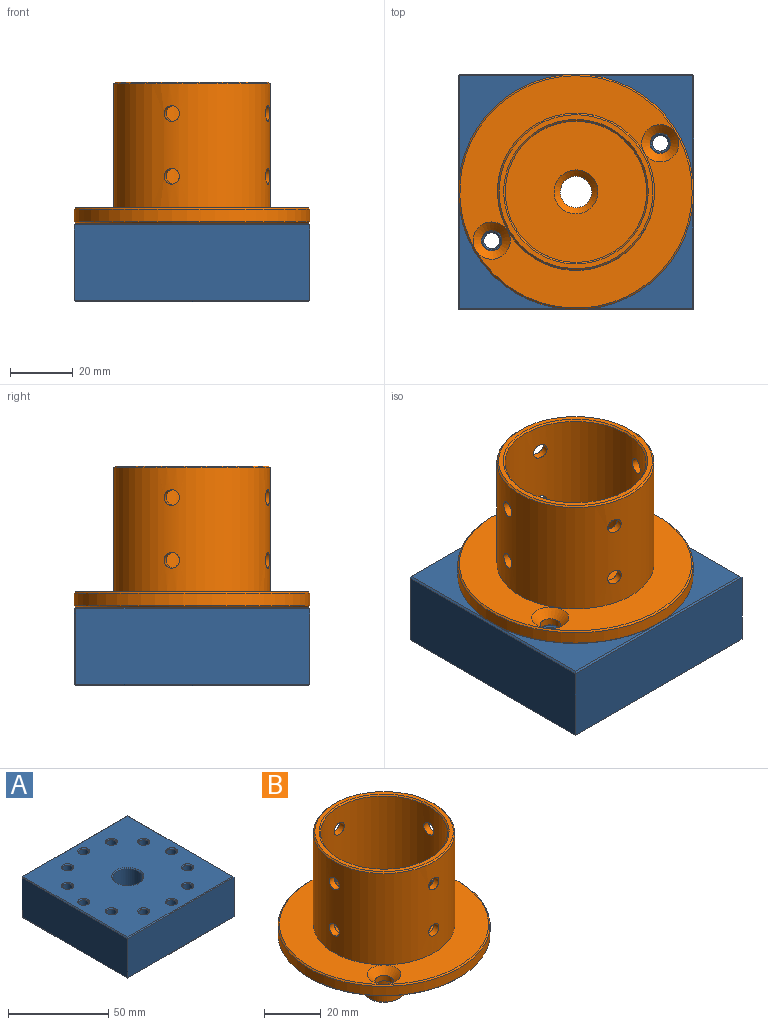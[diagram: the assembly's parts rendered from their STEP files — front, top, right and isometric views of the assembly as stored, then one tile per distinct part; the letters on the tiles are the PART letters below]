
ASSEMBLY  parts=2 mates=1
PART A: 59 faces, bbox 75x75x25 mm
  f0: plane 74x24mm, normal (0,1,0), area 1776mm2, adj f48,f52,f55,f58
  f1: plane 74.5x24mm, normal (-1,0,0), area 1788mm2, adj f2,f46,f52,f53
  f2: plane 75x24mm, normal (0,-1,0), area 1800mm2, adj f1,f4,f45,f50
  f3: cylinder r=7.5mm len=24mm, axis (0,0,-1), area 1131mm2, adj f43,f44
  f4: plane 74.5x24mm, normal (1,0,0), area 1788mm2, adj f2,f47,f54,f55
  f5: plane 74x74mm, normal (0,0,1), area 4935.6mm2, adj f31,f32,f33,f34,f35,f36,f37,f38
  f6: plane 74x74mm, normal (0,0,-1), area 4935.6mm2, adj f19,f20,f21,f22,f23,f24,f25,f26
  f7: cylinder r=2.5mm len=24mm, axis (0,0,1), area 377mm2, adj f20,f41
  f8: cylinder r=2.5mm len=24mm, axis (0,0,1), area 377mm2, adj f19,f42
  f9: cylinder r=2.5mm len=24mm, axis (0,0,1), area 377mm2, adj f30,f31
  f10: cylinder r=2.5mm len=24mm, axis (0,0,1), area 377mm2, adj f29,f32
  f11: cylinder r=2.5mm len=24mm, axis (0,0,1), area 377mm2, adj f21,f40
  f12: cylinder r=2.5mm len=24mm, axis (0,0,1), area 377mm2, adj f22,f39
  f13: cylinder r=2.5mm len=24mm, axis (0,0,1), area 377mm2, adj f23,f38
  f14: cylinder r=2.5mm len=24mm, axis (0,0,1), area 377mm2, adj f24,f37
  f15: cylinder r=2.5mm len=24mm, axis (0,0,1), area 377mm2, adj f25,f36
  f16: cylinder r=2.5mm len=24mm, axis (0,0,1), area 377mm2, adj f26,f35
  f17: cylinder r=2.5mm len=24mm, axis (0,0,1), area 377mm2, adj f27,f34
  f18: cylinder r=2.5mm len=24mm, axis (0,0,1), area 377mm2, adj f28,f33
  f19: cone r=3mm half-angle=45deg, axis (0,0,-1), area 12.2mm2, adj f6,f8
  f20: cone r=3mm half-angle=45deg, axis (0,0,-1), area 12.2mm2, adj f6,f7
  f21: cone r=3mm half-angle=45deg, axis (0,0,-1), area 12.2mm2, adj f6,f11
  f22: cone r=3mm half-angle=45deg, axis (0,0,-1), area 12.2mm2, adj f6,f12
  f23: cone r=3mm half-angle=45deg, axis (0,0,-1), area 12.2mm2, adj f6,f13
  f24: cone r=3mm half-angle=45deg, axis (0,0,-1), area 12.2mm2, adj f6,f14
  f25: cone r=3mm half-angle=45deg, axis (0,0,-1), area 12.2mm2, adj f6,f15
  f26: cone r=3mm half-angle=45deg, axis (0,0,-1), area 12.2mm2, adj f6,f16
  f27: cone r=3mm half-angle=45deg, axis (0,0,-1), area 12.2mm2, adj f6,f17
  f28: cone r=3mm half-angle=45deg, axis (0,0,-1), area 12.2mm2, adj f6,f18
  f29: cone r=3mm half-angle=45deg, axis (0,0,-1), area 12.2mm2, adj f6,f10
  f30: cone r=3mm half-angle=45deg, axis (0,0,-1), area 12.2mm2, adj f6,f9
  f31: cone r=2.5mm half-angle=45deg, axis (0,0,1), area 12.2mm2, adj f5,f9
  f32: cone r=2.5mm half-angle=45deg, axis (0,0,1), area 12.2mm2, adj f5,f10
  f33: cone r=2.5mm half-angle=45deg, axis (0,0,1), area 12.2mm2, adj f5,f18
  f34: cone r=2.5mm half-angle=45deg, axis (0,0,1), area 12.2mm2, adj f5,f17
  f35: cone r=2.5mm half-angle=45deg, axis (0,0,1), area 12.2mm2, adj f5,f16
  f36: cone r=2.5mm half-angle=45deg, axis (0,0,1), area 12.2mm2, adj f5,f15
  f37: cone r=2.5mm half-angle=45deg, axis (0,0,1), area 12.2mm2, adj f5,f14
  f38: cone r=2.5mm half-angle=45deg, axis (0,0,1), area 12.2mm2, adj f5,f13
  f39: cone r=2.5mm half-angle=45deg, axis (0,0,1), area 12.2mm2, adj f5,f12
  f40: cone r=2.5mm half-angle=45deg, axis (0,0,1), area 12.2mm2, adj f5,f11
  f41: cone r=2.5mm half-angle=45deg, axis (0,0,1), area 12.2mm2, adj f5,f7
  f42: cone r=2.5mm half-angle=45deg, axis (0,0,1), area 12.2mm2, adj f5,f8
  f43: cone r=8mm half-angle=45deg, axis (0,0,-1), area 34.4mm2, adj f3,f6
  f44: cone r=7.5mm half-angle=45deg, axis (0,0,1), area 34.4mm2, adj f3,f5
  f45: plane 75x0.5mm, normal (0,-0.71,0.71), area 52.7mm2, adj f2,f5,f46,f47
  f46: plane 74.5x0.5mm, normal (-0.71,0,0.71), area 52.5mm2, adj f1,f5,f45,f49
  f47: plane 74.5x0.5mm, normal (0.71,0,0.71), area 52.5mm2, adj f4,f5,f45,f51
  f48: plane 74x0.5mm, normal (0,0.71,0.71), area 52.3mm2, adj f0,f5,f49,f51
  f49: plane 0.5x0.5mm, normal (-0.58,0.58,0.58), area 0.2mm2, adj f46,f48,f52
  f50: plane 75x0.5mm, normal (0,-0.71,-0.71), area 52.7mm2, adj f2,f6,f53,f54
  f51: plane 0.5x0.5mm, normal (0.58,0.58,0.58), area 0.2mm2, adj f47,f48,f55
  f52: plane 24x0.5mm, normal (-0.71,0.71,0), area 17mm2, adj f0,f1,f49,f56
  f53: plane 74.5x0.5mm, normal (-0.71,0,-0.71), area 52.5mm2, adj f1,f6,f50,f56
  f54: plane 74.5x0.5mm, normal (0.71,0,-0.71), area 52.5mm2, adj f4,f6,f50,f57
  f55: plane 24x0.5mm, normal (0.71,0.71,0), area 17mm2, adj f0,f4,f51,f57
  f56: plane 0.5x0.5mm, normal (-0.58,0.58,-0.58), area 0.2mm2, adj f52,f53,f58
  f57: plane 0.5x0.5mm, normal (0.58,0.58,-0.58), area 0.2mm2, adj f54,f55,f58
  f58: plane 74x0.5mm, normal (0,0.71,-0.71), area 52.3mm2, adj f0,f6,f56,f57
PART B: 29 faces, bbox 75x75x69 mm
  f0: cylinder r=22.5mm len=45mm, axis (0,0,-1), area 5426.6mm2, adj f2,f12,f13,f14,f15,f16,f17,f18
  f1: cylinder r=25mm len=50mm, axis (0,0,-1), area 6047.1mm2, adj f5,f12,f13,f14,f15,f16,f17,f18
  f2: plane 45x45mm, normal (0,0,1), area 1436.5mm2, adj f0,f22
  f3: cylinder r=37.5mm len=75mm, axis (0,0,-1), area 942.5mm2, adj f25,f26
  f4: cylinder r=5mm len=26.5mm, axis (0,0,-1), area 832.5mm2, adj f22,f23
  f5: plane 74x74mm, normal (0,0,1), area 2116.4mm2, adj f1,f8,f10,f26
  f6: plane 74x74mm, normal (0,0,-1), area 4057.8mm2, adj f7,f9,f20,f25
  f7: cylinder r=3.25mm len=6.5mm, axis (0,0,1), area 47.4mm2, adj f6,f8
  f8: cone r=3.25mm half-angle=45deg, axis (0,0,1), area 109.3mm2, adj f5,f7
  f9: cylinder r=3.25mm len=6.5mm, axis (0,0,1), area 47.4mm2, adj f6,f10
  f10: cone r=3.25mm half-angle=45deg, axis (0,0,1), area 109.3mm2, adj f5,f9
  f11: plane 49x49mm, normal (0,0,1), area 223.8mm2, adj f27,f28
  f12: cylinder r=2.5mm len=5mm, axis (1,0,0), area 39.4mm2, adj f0,f1
  f13: cylinder r=2.5mm len=5mm, axis (1,0,0), area 39.4mm2, adj f0,f1
  f14: cylinder r=2.5mm len=5mm, axis (0,1,0), area 39.4mm2, adj f0,f1
  f15: cylinder r=2.5mm len=5mm, axis (0,1,0), area 39.4mm2, adj f0,f1
  f16: cylinder r=2.5mm len=5mm, axis (-1,0,0), area 39.4mm2, adj f0,f1
  f17: cylinder r=2.5mm len=5mm, axis (-1,0,0), area 39.4mm2, adj f0,f1
  f18: cylinder r=2.5mm len=5mm, axis (0,-1,0), area 39.4mm2, adj f0,f1
  f19: cylinder r=2.5mm len=5mm, axis (0,-1,0), area 39.4mm2, adj f0,f1
  f20: cylinder r=7.5mm len=23.5mm, axis (0,0,-1), area 1107.4mm2, adj f6,f24
  f21: plane 14x14mm, normal (0,0,-1), area 58.9mm2, adj f23,f24
  f22: cone r=5mm half-angle=45deg, axis (0,0,1), area 106.6mm2, adj f2,f4
  f23: cone r=5.5mm half-angle=45deg, axis (0,0,-1), area 23.3mm2, adj f4,f21
  f24: cone r=7.5mm half-angle=45deg, axis (0,0,1), area 32.2mm2, adj f20,f21
  f25: cone r=37.5mm half-angle=45deg, axis (0,0,1), area 165.5mm2, adj f3,f6
  f26: cone r=37mm half-angle=45deg, axis (0,0,-1), area 165.5mm2, adj f3,f5
  f27: cone r=24.5mm half-angle=45deg, axis (0,0,-1), area 110mm2, adj f1,f11
  f28: cone r=22.5mm half-angle=45deg, axis (0,0,1), area 101.1mm2, adj f0,f11
PLACE A t=(1.44,7.05,54.43)mm
PLACE B rot(axis=(0,0,-1),15deg) t=(1.44,7.05,55.43)mm
MATE cylindrical A.f3 <-> B.f20  axis (0,0,1) through (1.44,7.05,79.43)mm
